# Revit family: Keilhauer_Juxta_Lounge_High_Chair
name_source: partatom
category: Furniture
units: mm (PartAtom-declared; Revit-internal decimal feet)

## family parameters
Always vertical = Yes
Cut with Voids When Loaded = No
OmniClass Number = 23.40.70.14.64.11
OmniClass Title = Office Furniture
Room Calculation Point = No
Shared = No
Work Plane-Based = No

## types (6) — shared parameters
Assembly Code = E2020200
Catalog = JUXTA
Manufacturer = Keilhauer, Corp.
Product Documentation Link = http://www.keilhauer.com
URL = http://www.keilhauer.com
zero-valued in all types: Default Elevation

## per-type parameters (varying)
| type | Five Star | Four Leg | Four Star | Model | Not Tablet | Sled Base | Tablet |
| High Back Armless Chair with 4 Leg Base, Lounge Height | No | Yes | No | 45420 | Yes | No | No |
| High Back Armless Lounge Chair with Sled Base | No | No | No | 45430 | Yes | Yes | No |
| High Back Armless Lounge Chair with 4 Star Base and Glides | No | No | Yes | 45440 | Yes | No | No |
| High Back Armless Lounge Chair with 4 Star Base and Tablet | No | No | Yes | 45441 | No | No | Yes |
| High Back Armless Lounge Chair with 5 Star Base and Casters | Yes | No | No | 45450 | Yes | No | No |
| High Back Armless Lounge Chair with 5 Star Base and Tablet | Yes | No | No | 45451 | No | No | Yes |

note: column(s) folded — value = type name in every type: Description

## geometry (parser evidence)
native form markers: Sweep x6
no freeform markers — native parametric forms only
